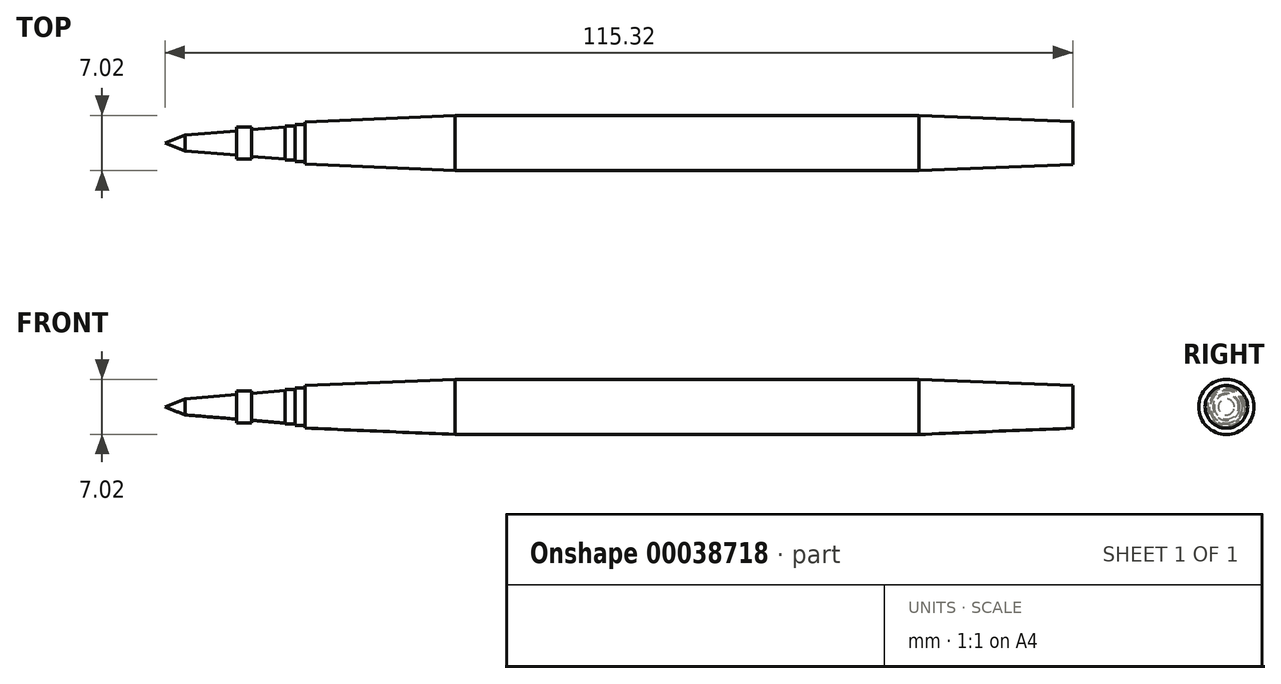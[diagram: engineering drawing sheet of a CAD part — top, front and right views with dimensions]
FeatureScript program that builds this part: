
annotation { "Feature Type Name" : "Feature", "Feature Type Description" : "" }
export const myFeature = defineFeature(function(context is Context, id is Id, definition is map)
    precondition{}
    {
        {
            var Q0;
            Q0=qCreatedBy(makeId("Front.planeOp"),FACE);
            var sketch = newSketch(context, id + "F0", { "sketchPlane" : qUnion([Q0])});
            skLineSegment(sketch, "E0", {"start": v(0, 0) * mm, "end": v(2.54, -1.02) * mm});
            skLineSegment(sketch, "E1", {"start": v(2.54, -1.02) * mm, "end": v(9.1, -1.55) * mm});
            skLineSegment(sketch, "E2", {"start": v(15.24, -2.06) * mm, "end": v(15.24, -2.18) * mm});
            skLineSegment(sketch, "E3", {"start": v(15.24, -2.18) * mm, "end": v(16.51, -2.18) * mm});
            skLineSegment(sketch, "E4", {"start": v(16.51, -2.18) * mm, "end": v(16.51, -2.37) * mm});
            skLineSegment(sketch, "E5", {"start": v(16.51, -2.37) * mm, "end": v(17.78, -2.37) * mm});
            skLineSegment(sketch, "E6", {"start": v(17.78, -2.37) * mm, "end": v(17.78, -2.7) * mm});
            skLineSegment(sketch, "E7", {"start": v(17.78, -2.7) * mm, "end": v(36.83, -3.5) * mm});
            skLineSegment(sketch, "E8", {"start": v(36.83, -3.5) * mm, "end": v(95.76, -3.5) * mm});
            skLineSegment(sketch, "E9", {"start": v(95.76, -3.5) * mm, "end": v(115.32, -2.7) * mm});
            skLineSegment(sketch, "E10", {"start": v(115.32, -2.7) * mm, "end": v(115.32, 0) * mm});
            skLineSegment(sketch, "E11", {"start": v(115.32, 0) * mm, "end": v(0, 0) * mm});
            skLineSegment(sketch, "E12", {"start": v(9.1, -1.55) * mm, "end": v(9.1, -2.03) * mm});
            skLineSegment(sketch, "E13", {"start": v(9.1, -2.03) * mm, "end": v(11, -2.03) * mm});
            skLineSegment(sketch, "E14", {"start": v(11, -2.03) * mm, "end": v(11, -1.7) * mm});
            skLineSegment(sketch, "E15.trimOffspring", {"start": v(11, -1.7) * mm, "end": v(15.24, -2.06) * mm});
            skSolve(sketch);
        }
        {
            var Q0;
            Q0=makeQuery(id+"F0.imprint","IMPRINT",FACE,{"disambiguationData":[TD([[makeQuery(id+"F0.imprint","IMPRINT",EDGE,{"derivedFrom":sQuery(id+"F0.wireOp",EDGE,"E0")}),1.0]])]});
            var Q1;
            Q1=sQuery(id+"F0.wireOp",EDGE,"E11");
            revolve(context, id + "F1", {"entities" : qUnion([Q0]), "axis" : qUnion([Q1]), "revolveType" : RevolveType.FULL});
        }
    });
